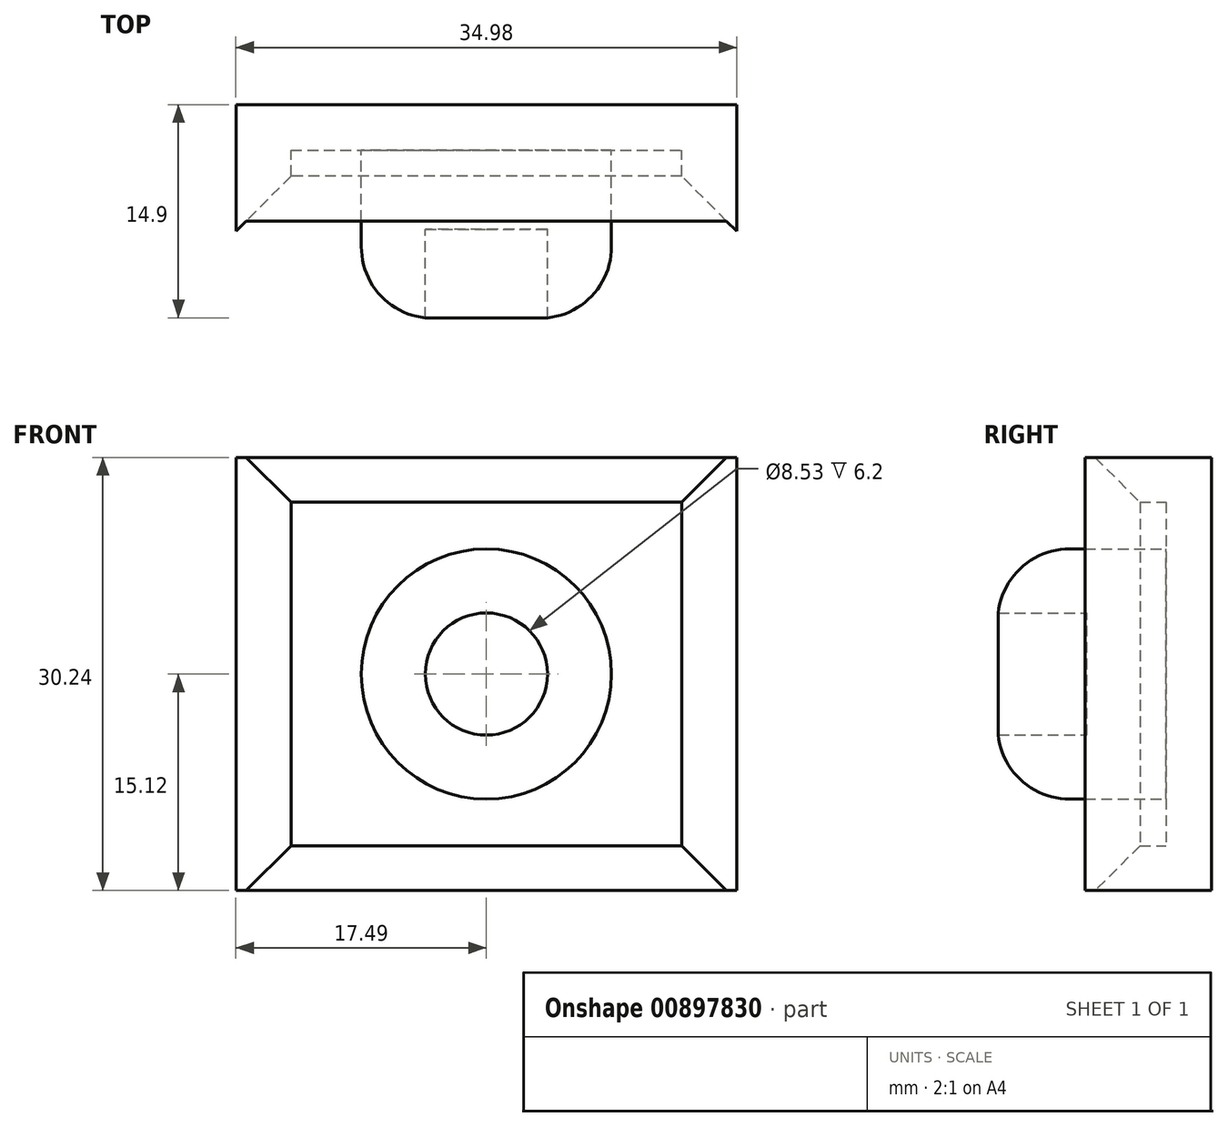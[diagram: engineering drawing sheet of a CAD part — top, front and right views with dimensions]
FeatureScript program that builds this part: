
annotation { "Feature Type Name" : "Feature", "Feature Type Description" : "" }
export const myFeature = defineFeature(function(context is Context, id is Id, definition is map)
    precondition{}
    {
        {
            var Q0;
            Q0=qCreatedBy(makeId("Front.planeOp"),FACE);
            var sketch = newSketch(context, id + "F0", { "sketchPlane" : qUnion([Q0])});
            skLineSegment(sketch, "E0.bottom", {"start": v(17.49, -15.12) * mm, "end": v(-17.49, -15.12) * mm});
            skLineSegment(sketch, "E0.top", {"start": v(17.49, 15.12) * mm, "end": v(-17.49, 15.12) * mm});
            skLineSegment(sketch, "E0.left", {"start": v(17.49, -15.12) * mm, "end": v(17.49, 15.12) * mm});
            skLineSegment(sketch, "E0.right", {"start": v(-17.49, -15.12) * mm, "end": v(-17.49, 15.12) * mm});
            skPoint(sketch, "E0.middle", {"position": v(0, 0) * mm});
            skLineSegment(sketch, "E1.bottom", {"start": v(-13.64, 12) * mm, "end": v(13.64, 12) * mm});
            skLineSegment(sketch, "E1.top", {"start": v(-13.64, -12) * mm, "end": v(13.64, -12) * mm});
            skLineSegment(sketch, "E1.left", {"start": v(-13.64, 12) * mm, "end": v(-13.64, -12) * mm});
            skLineSegment(sketch, "E1.right", {"start": v(13.64, 12) * mm, "end": v(13.64, -12) * mm});
            skSolve(sketch);
        }
        {
            var Q0;
            Q0=makeQuery(id+"F0.imprint","IMPRINT",FACE,{"disambiguationData":[TD([[makeQuery(id+"F0.imprint","IMPRINT",EDGE,{"derivedFrom":sQuery(id+"F0.wireOp",EDGE,"E1.bottom")}),-1.0]])]});
            extrude(context, id + "F1", {"entities" : qUnion([Q0]), "depth" : 3.2 * mm, "offsetDistance" : 25 * mm});
        }
        {
            var Q0;
            Q0=makeQuery(id+"F1.opExtrude","CAP_FACE",FACE,{"disambiguationData":[OSD([sQuery(id+"F0.wireOp",EDGE,"E1.bottom"),sQuery(id+"F0.wireOp",EDGE,"E1.top"),sQuery(id+"F0.wireOp",EDGE,"E1.left"),sQuery(id+"F0.wireOp",EDGE,"E1.right")])],"isStart":false});
            var sketch = newSketch(context, id + "F2", { "sketchPlane" : qUnion([Q0])});
            skCircle(sketch, "E2", {"center": v(0, 0) * mm, "radius": 8.73 * mm});
            skSolve(sketch);
        }
        {
            var Q0;
            Q0=makeQuery(id+"F2.imprint","IMPRINT",FACE,{"disambiguationData":[TD([[makeQuery(id+"F2.imprint","IMPRINT",EDGE,{"derivedFrom":sQuery(id+"F2.wireOp",EDGE,"E2")}),1.0]])]});
            extrude(context, id + "F3", {"entities" : qUnion([Q0]), "operationType" : NewBodyOperationType.ADD, "depth" : 5.5 * mm, "offsetDistance" : 25 * mm});
        }
        {
            var Q0;
            Q0 = qSketchRegion(id + "F0", true);
            var Q1;
            Q1 = qSketchRegion(id + "F5", true);
            extrude(context, id + "F4", {"entities" : qUnion([Q0, Q1]), "operationType" : NewBodyOperationType.ADD, "depth" : 15 * mm, "offsetDistance" : 25 * mm});
        }
        {
            var Q0;
            Q0=makeQuery(id+"F3.opExtrude","CAP_FACE",FACE,{"disambiguationData":[OSD([sQuery(id+"F2.wireOp",EDGE,"E2")])],"isStart":false});
            var sketch = newSketch(context, id + "F5", { "sketchPlane" : qUnion([Q0])});
            skCircle(sketch, "E3", {"center": v(0, 0) * mm, "radius": 4.27 * mm});
            skLineSegment(sketch, "E4.bottom", {"start": v(-9.16, 9.34) * mm, "end": v(9.16, 9.34) * mm, "construction": true});
            skLineSegment(sketch, "E4.top", {"start": v(-9.16, -9.34) * mm, "end": v(9.16, -9.34) * mm, "construction": true});
            skLineSegment(sketch, "E4.left", {"start": v(-9.16, 9.34) * mm, "end": v(-9.16, -9.34) * mm, "construction": true});
            skLineSegment(sketch, "E4.right", {"start": v(9.16, 9.34) * mm, "end": v(9.16, -9.34) * mm, "construction": true});
            skSolve(sketch);
        }
        {
            var Q0;
            Q0=makeQuery(id+"F5.imprint","IMPRINT",FACE,{"disambiguationData":[TD([[makeQuery(id+"F5.imprint","IMPRINT",EDGE,{"derivedFrom":sQuery(id+"F5.wireOp",EDGE,"E3")}),-1.0]])]});
            extrude(context, id + "F6", {"entities" : qUnion([Q0]), "operationType" : NewBodyOperationType.ADD, "depth" : 6.2 * mm, "offsetDistance" : 25 * mm});
        }
        {
            var Q0;
            Q0=makeQuery(id+"F3.opExtrude","CAP_EDGE",EDGE,{"disambiguationData":[OSD([sQuery(id+"F2.wireOp",EDGE,"E2")])],"isStart":true});
            var Q1;
            Q1=makeQuery(id+"F6.opExtrude","CAP_EDGE",EDGE,{"disambiguationData":[OSD([sQuery(id+"F2.wireOp",EDGE,"E2")])],"isStart":false});
            fillet(context, id + "F7", {"entities" : qUnion([Q0, Q1]), "radius" : 5 * mm, "tangentPropagation" : true, "allowEdgeOverflow" : false});
        }
        {
            var Q0;
            Q0=makeQuery(id+"F4.opExtrude","CAP_EDGE",EDGE,{"disambiguationData":[OSD([sQuery(id+"F0.wireOp",EDGE,"E1.left")])],"isStart":false});
            var Q1;
            Q1=makeQuery(id+"F4.opExtrude","CAP_EDGE",EDGE,{"disambiguationData":[OSD([sQuery(id+"F0.wireOp",EDGE,"E1.right")])],"isStart":false});
            var Q2;
            Q2=makeQuery(id+"F4.opExtrude","CAP_EDGE",EDGE,{"disambiguationData":[OSD([sQuery(id+"F0.wireOp",EDGE,"E1.top")])],"isStart":false});
            var Q3;
            Q3=makeQuery(id+"F4.opExtrude","CAP_EDGE",EDGE,{"disambiguationData":[OSD([sQuery(id+"F0.wireOp",EDGE,"E1.bottom")])],"isStart":false});
            chamfer(context, id + "F8", {"entities" : qUnion([Q0, Q1, Q2, Q3]), "width" : 10 * mm, "tangentPropagation" : true});
        }
    });
